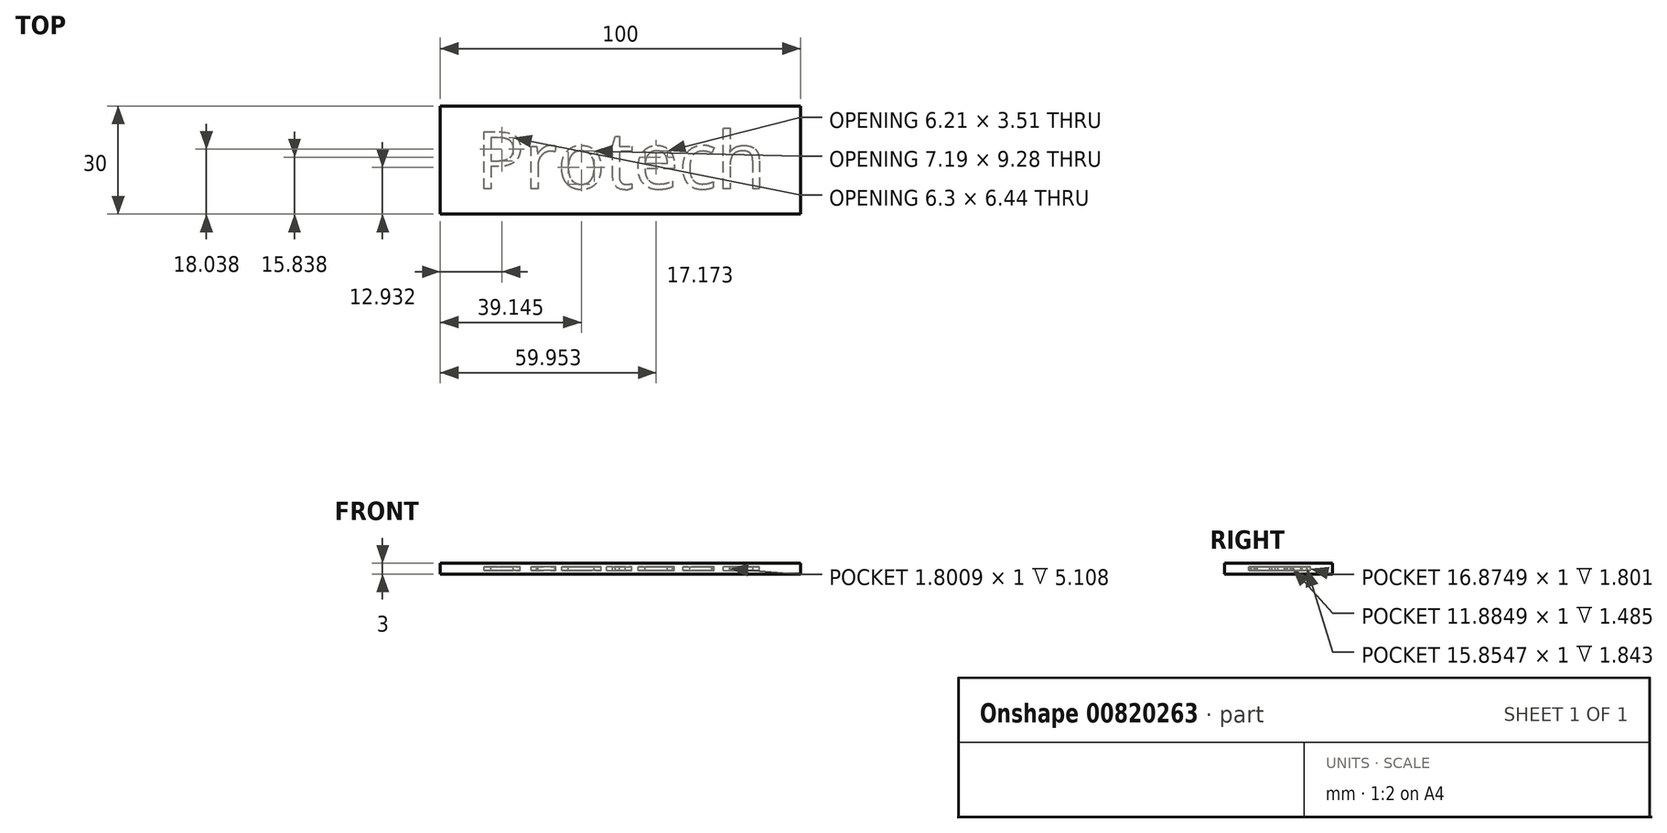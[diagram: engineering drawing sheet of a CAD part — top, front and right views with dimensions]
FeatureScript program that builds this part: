
annotation { "Feature Type Name" : "Feature", "Feature Type Description" : "" }
export const myFeature = defineFeature(function(context is Context, id is Id, definition is map)
    precondition{}
    {
        {
            var Q0;
            Q0=qCreatedBy(makeId("Top.planeOp"),FACE);
            var sketch = newSketch(context, id + "F0", { "sketchPlane" : qUnion([Q0])});
            skLineSegment(sketch, "E0.bottom", {"start": v(-52.64, 24.37) * mm, "end": v(47.36, 24.37) * mm});
            skLineSegment(sketch, "E0.top", {"start": v(-52.64, -5.63) * mm, "end": v(47.36, -5.63) * mm});
            skLineSegment(sketch, "E0.left", {"start": v(-52.64, 24.37) * mm, "end": v(-52.64, -5.63) * mm});
            skLineSegment(sketch, "E0.right", {"start": v(47.36, 24.37) * mm, "end": v(47.36, -5.63) * mm});
            skText(sketch, "E1", { "text": "Protech", "fontName": "OpenSans-Regular.ttf"});
            const initialGuessF0  = {"E1": [-0.04264, 0.00137, 1, 0, 0.01599]};
            skSetInitialGuess(sketch, initialGuessF0);
            skSolve(sketch);
        }
        {
            var Q0;
            Q0=makeQuery(id+"F0.imprint","IMPRINT",FACE,{"disambiguationData":[TD([[makeQuery(id+"F0.imprint","IMPRINT",EDGE,{"derivedFrom":sQuery(id+"F0.wireOp",EDGE,"E0.bottom")}),-1.0]])]});
            var Q1;
            Q1=makeQuery(id+"F0.imprint","IMPRINT",FACE,{"disambiguationData":[TD([[makeQuery(id+"F0.imprint","IMPRINT",EDGE,{"derivedFrom":sQuery(id+"F0.wireOp",EDGE,"E1.sketch_text.stroke-0")}),-1.0]])]});
            var Q2;
            Q2=makeQuery(id+"F0.imprint","IMPRINT",FACE,{"disambiguationData":[TD([[makeQuery(id+"F0.imprint","IMPRINT",EDGE,{"derivedFrom":sQuery(id+"F0.wireOp",EDGE,"E1.sketch_text.stroke-8")}),1.0]])]});
            var Q3;
            Q3=makeQuery(id+"F0.imprint","IMPRINT",FACE,{"disambiguationData":[TD([[makeQuery(id+"F0.imprint","IMPRINT",EDGE,{"derivedFrom":sQuery(id+"F0.wireOp",EDGE,"E1.sketch_text.stroke-15")}),-1.0]])]});
            var Q4;
            Q4=makeQuery(id+"F0.imprint","IMPRINT",FACE,{"disambiguationData":[TD([[makeQuery(id+"F0.imprint","IMPRINT",EDGE,{"derivedFrom":sQuery(id+"F0.wireOp",EDGE,"E1.sketch_text.stroke-28")}),-1.0]])]});
            var Q5;
            Q5=makeQuery(id+"F0.imprint","IMPRINT",FACE,{"disambiguationData":[TD([[makeQuery(id+"F0.imprint","IMPRINT",EDGE,{"derivedFrom":sQuery(id+"F0.wireOp",EDGE,"E1.sketch_text.stroke-37")}),1.0]])]});
            var Q6;
            Q6=makeQuery(id+"F0.imprint","IMPRINT",FACE,{"disambiguationData":[TD([[makeQuery(id+"F0.imprint","IMPRINT",EDGE,{"derivedFrom":sQuery(id+"F0.wireOp",EDGE,"E1.sketch_text.stroke-45")}),-1.0]])]});
            var Q7;
            Q7=makeQuery(id+"F0.imprint","IMPRINT",FACE,{"disambiguationData":[TD([[makeQuery(id+"F0.imprint","IMPRINT",EDGE,{"derivedFrom":sQuery(id+"F0.wireOp",EDGE,"E1.sketch_text.stroke-78")}),1.0]])]});
            var Q8;
            Q8=makeQuery(id+"F0.imprint","IMPRINT",FACE,{"disambiguationData":[TD([[makeQuery(id+"F0.imprint","IMPRINT",EDGE,{"derivedFrom":sQuery(id+"F0.wireOp",EDGE,"E1.sketch_text.stroke-64")}),-1.0]])]});
            var Q9;
            Q9=makeQuery(id+"F0.imprint","IMPRINT",FACE,{"disambiguationData":[TD([[makeQuery(id+"F0.imprint","IMPRINT",EDGE,{"derivedFrom":sQuery(id+"F0.wireOp",EDGE,"E1.sketch_text.stroke-83")}),-1.0]])]});
            var Q10;
            Q10=makeQuery(id+"F0.imprint","IMPRINT",FACE,{"disambiguationData":[TD([[makeQuery(id+"F0.imprint","IMPRINT",EDGE,{"derivedFrom":sQuery(id+"F0.wireOp",EDGE,"E1.sketch_text.stroke-98")}),-1.0]])]});
            extrude(context, id + "F1", {"entities" : qUnion([Q0, Q1, Q2, Q3, Q4, Q5, Q6, Q7, Q8, Q9, Q10]), "oppositeDirection" : true, "depth" : 2 * mm, "offsetDistance" : 25 * mm});
        }
        {
            var Q0;
            Q0=makeQuery(id+"F0.imprint","IMPRINT",FACE,{"disambiguationData":[TD([[makeQuery(id+"F0.imprint","IMPRINT",EDGE,{"derivedFrom":sQuery(id+"F0.wireOp",EDGE,"E1.sketch_text.stroke-0")}),-1.0]])]});
            var Q1;
            Q1=makeQuery(id+"F0.imprint","IMPRINT",FACE,{"disambiguationData":[TD([[makeQuery(id+"F0.imprint","IMPRINT",EDGE,{"derivedFrom":sQuery(id+"F0.wireOp",EDGE,"E1.sketch_text.stroke-15")}),-1.0]])]});
            var Q2;
            Q2=makeQuery(id+"F0.imprint","IMPRINT",FACE,{"disambiguationData":[TD([[makeQuery(id+"F0.imprint","IMPRINT",EDGE,{"derivedFrom":sQuery(id+"F0.wireOp",EDGE,"E1.sketch_text.stroke-28")}),-1.0]])]});
            var Q3;
            Q3=makeQuery(id+"F0.imprint","IMPRINT",FACE,{"disambiguationData":[TD([[makeQuery(id+"F0.imprint","IMPRINT",EDGE,{"derivedFrom":sQuery(id+"F0.wireOp",EDGE,"E1.sketch_text.stroke-45")}),-1.0]])]});
            var Q4;
            Q4=makeQuery(id+"F0.imprint","IMPRINT",FACE,{"disambiguationData":[TD([[makeQuery(id+"F0.imprint","IMPRINT",EDGE,{"derivedFrom":sQuery(id+"F0.wireOp",EDGE,"E1.sketch_text.stroke-64")}),-1.0]])]});
            var Q5;
            Q5=makeQuery(id+"F0.imprint","IMPRINT",FACE,{"disambiguationData":[TD([[makeQuery(id+"F0.imprint","IMPRINT",EDGE,{"derivedFrom":sQuery(id+"F0.wireOp",EDGE,"E1.sketch_text.stroke-83")}),-1.0]])]});
            var Q6;
            Q6=makeQuery(id+"F0.imprint","IMPRINT",FACE,{"disambiguationData":[TD([[makeQuery(id+"F0.imprint","IMPRINT",EDGE,{"derivedFrom":sQuery(id+"F0.wireOp",EDGE,"E1.sketch_text.stroke-98")}),-1.0]])]});
            extrude(context, id + "F2", {"entities" : qUnion([Q0, Q1, Q2, Q3, Q4, Q5, Q6]), "operationType" : NewBodyOperationType.REMOVE, "oppositeDirection" : true, "depth" : 1 * mm, "offsetDistance" : 25 * mm});
        }
        {
            var Q0;
            Q0=makeQuery(id+"F0.imprint","IMPRINT",FACE,{"disambiguationData":[TD([[makeQuery(id+"F0.imprint","IMPRINT",EDGE,{"derivedFrom":sQuery(id+"F0.wireOp",EDGE,"E0.bottom")}),-1.0]])]});
            var sketch = newSketch(context, id + "F3", { "sketchPlane" : qUnion([Q0])});
            skLineSegment(sketch, "E2.bottom", {"start": v(-52.64, -5.63) * mm, "end": v(47.36, -5.63) * mm});
            skLineSegment(sketch, "E2.top", {"start": v(-52.64, 24.37) * mm, "end": v(47.36, 24.37) * mm});
            skLineSegment(sketch, "E2.left", {"start": v(-52.64, -5.63) * mm, "end": v(-52.64, 24.37) * mm});
            skLineSegment(sketch, "E2.right", {"start": v(47.36, -5.63) * mm, "end": v(47.36, 24.37) * mm});
            skSolve(sketch);
        }
        {
            var Q0;
            Q0 = qSketchRegion(id + "F3", true);
            extrude(context, id + "F4", {"entities" : qUnion([Q0]), "operationType" : NewBodyOperationType.ADD, "depth" : 1 * mm, "offsetDistance" : 25 * mm});
        }
    });
